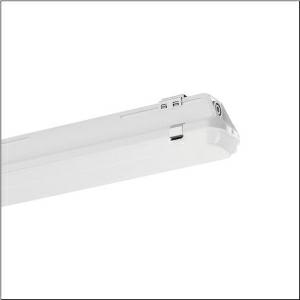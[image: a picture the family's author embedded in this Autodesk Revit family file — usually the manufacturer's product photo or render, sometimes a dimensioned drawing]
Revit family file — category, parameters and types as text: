
# Revit family: monsun_r__11_emergency_51fp10dp468l2_17f5
name_source: partatom
category: Lighting Fixtures
units: mm (PartAtom-declared; Revit-internal decimal feet)

## family parameters
Cut with Voids When Loaded = No
Host = Face
Light Source = No
Part Type = Normal
Room Calculation Point = No
Round Connector Dimension = Use Diameter
Shared = No

## types (1)
- --- (1 x LED, 950 lm, 5.9 W, 4000K)
    Apparent Load = 6 VA
    CIE Flux Codes = 47 77 93 94 100
    Color Rendering = 80
    Color Temperature = 4000K
    Default Elevation = 1800 mm
    Description = Monsun® 11 emergency, damp-proof luminaire, chain hanger, primary optical cover: enclosure, of PMMA, light emission: direct distribution, primary light characteristic: symmetric, installation type: suspended mounting, surface-mounted, horizontal mounting, vertical mounting, LED, rated luminous flux: 6.050lm, luminous efficacy: 192lm/W, light colour: 840, colour temperature: 4000K, control gear: DALI 2, with terminal, 5-pole, max. 2.5mm², mains connection: 220..240V, AC/DC, 0/50..60Hz, rated input power: 32W, luminaire housing, of glass-fibre reinforced polyester, uncoated, bright grey, incl. chain hanger, length: 1.590mm, width: 90mm, height: 88mm, clip for enclosure, of stainless steel (V2A), ceiling mounting element, of stainless steel (V2A), chain hanger, of stainless steel (V2A), protection rating (complete): IP66, insulation class (complete): insulation class I (protective earthing), certification: CE, UKCA, protection symbol: D, impact resistance: IK04, permissible operating ambient temperature: -25..+40°C, standard: EN 50419, EN 60598-2-1, EN 60598-2-22, corresponds to IFS (International Featured Standards) requirements for safety and quality in the food industry, for indoor or canopied outdoor use, no direct snow, no direct sun, no direct rain, LABS conformity tested according to VDMA 24364:2018-05, contact your sales advisor before using the luminaires in applications with unclear chemical exposure, large temperature fluctuations or condensation-forming humidity, packaging unit: 1 piece
    Height = 89 mm
    Lamp = 1 x LED
    Lamp Light Flux = 950 lm
    Lamp Power = 5.9 W
    Lamp count = 1
    Length = 1590 mm
    Luminous efficacy = 161 lm/W
    Manufacturer = Siteco
    ModVariant = No
    Model = 51FP10DP468L2
    Mounting Place = Ceiling
    Mounting Type = Surface mounted
    Number of Poles = 1
    OnlyDefault = Yes
    Power Factor = 1
    Product Name = Monsun® 11 emergency
    Product group = damp-proof luminaire
    ProductGroupID = 301
    Protection Class = Protection class I
    Protection Degree = IP 66
    RLX_Detail_Level = 1
    RLX_Emergency_Light_Flux = 0 lm
    RLX_Emergency_Type = 0
    RLX_Emergency_Type_DB = No
    RlxData = <blob elided: 92421 chars, md5=aac8fb3e>
    Socket = socket
    Standby Power = 0 W
    System Light Flux = 950 lm
    System Power = 6 W
    Type Comments = : DC mode (central or group accumulator) initial emergency light level
    Type Image = l_1349237.jpg
    URL = http://relux.com
    VarID = @adj_037917
    Voltage = 0 V
    Weight = 0.00 kg
    Width = 90 mm

## geometry (parser evidence)
native form markers: Blend x4, Sweep x14
no freeform markers — native parametric forms only
